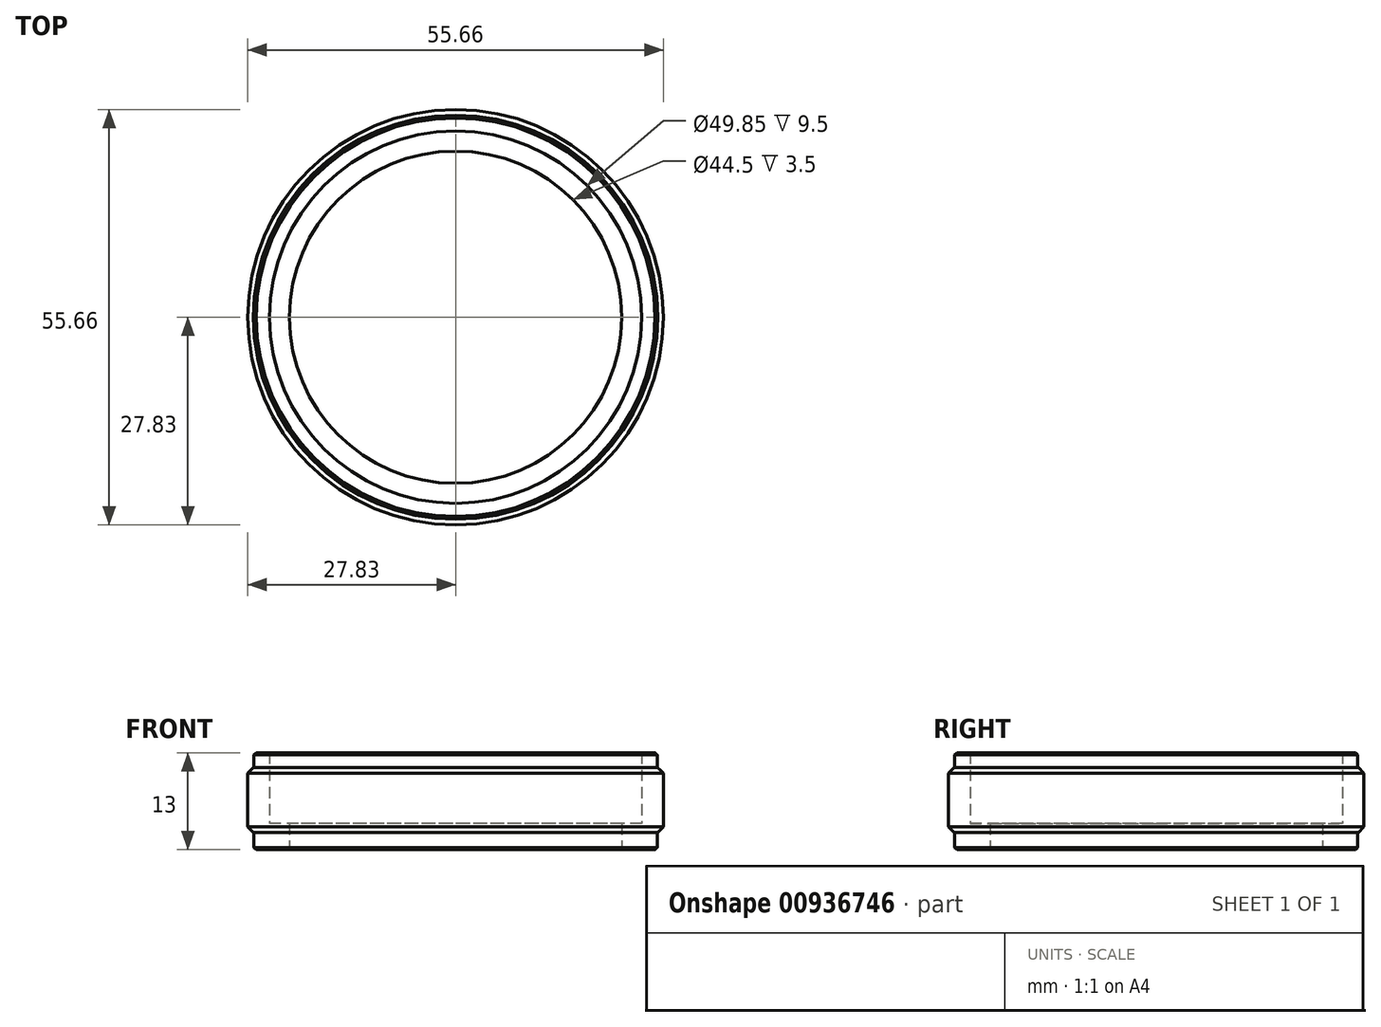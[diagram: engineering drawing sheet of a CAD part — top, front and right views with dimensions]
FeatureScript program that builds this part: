
annotation { "Feature Type Name" : "Feature", "Feature Type Description" : "" }
export const myFeature = defineFeature(function(context is Context, id is Id, definition is map)
    precondition{}
    {
        {
            var Q0;
            Q0=qCreatedBy(makeId("Top.planeOp"),FACE);
            var sketch = newSketch(context, id + "F0", { "sketchPlane" : qUnion([Q0])});
            skCircle(sketch, "E0", {"center": v(0, 0) * mm, "radius": 22.25 * mm});
            skCircle(sketch, "E1", {"center": v(0, 0) * mm, "radius": 27 * mm});
            skCircle(sketch, "E2", {"center": v(0, 0) * mm, "radius": 27.82 * mm});
            skCircle(sketch, "E3", {"center": v(0, 0) * mm, "radius": 24.93 * mm});
            skSolve(sketch);
        }
        {
            var Q0;
            Q0=makeQuery(id+"F0.imprint","IMPRINT",FACE,{"disambiguationData":[TD([[makeQuery(id+"F0.imprint","IMPRINT",EDGE,{"derivedFrom":sQuery(id+"F0.wireOp",EDGE,"E1")}),1.0]])]});
            extrude(context, id + "F1", {"entities" : qUnion([Q0]), "depth" : 13 * mm, "offsetDistance" : 25 * mm});
        }
        {
            var Q0;
            Q0=makeQuery(id+"F0.imprint","IMPRINT",FACE,{"disambiguationData":[TD([[makeQuery(id+"F0.imprint","IMPRINT",EDGE,{"derivedFrom":sQuery(id+"F0.wireOp",EDGE,"E0")}),-1.0]])]});
            extrude(context, id + "F2", {"entities" : qUnion([Q0]), "operationType" : NewBodyOperationType.ADD, "depth" : 3.5 * mm, "offsetDistance" : 25 * mm});
        }
        {
            var Q0;
            Q0=makeQuery(id+"F0.imprint","IMPRINT",FACE,{"disambiguationData":[TD([[makeQuery(id+"F0.imprint","IMPRINT",EDGE,{"derivedFrom":sQuery(id+"F0.wireOp",EDGE,"E1")}),-1.0]])]});
            extrude(context, id + "F3", {"entities" : qUnion([Q0]), "operationType" : NewBodyOperationType.ADD, "depth" : 11 * mm, "offsetDistance" : 25 * mm, "hasSecondDirection" : true, "secondDirectionOppositeDirection" : true, "secondDirectionDepth" : -2.3 * mm});
        }
        {
            var Q0;
            Q0=makeQuery(id+"F1.opExtrude","CAP_EDGE",EDGE,{"disambiguationData":[OSD([sQuery(id+"F0.wireOp",EDGE,"E1")])],"isStart":false});
            var Q1;
            Q1=makeQuery(id+"F1.opExtrude","CAP_EDGE",EDGE,{"disambiguationData":[OSD([sQuery(id+"F0.wireOp",EDGE,"E1")])],"isStart":true});
            chamfer(context, id + "F4", {"entities" : qUnion([Q0, Q1]), "width" : .3 * mm, "tangentPropagation" : true});
        }
        {
            var Q0;
            Q0=makeQuery(id+"F3.opExtrude","SWEPT_FACE",FACE,{"disambiguationData":[OSD([sQuery(id+"F0.wireOp",EDGE,"E2")])]});
            chamfer(context, id + "F5", {"entities" : qUnion([Q0]), "width" : .75 * mm, "tangentPropagation" : true});
        }
    });
